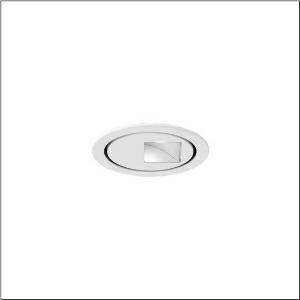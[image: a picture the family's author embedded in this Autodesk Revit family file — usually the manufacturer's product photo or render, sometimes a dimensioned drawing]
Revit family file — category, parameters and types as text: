
# Revit family: lunis_11_micro_round_51dj11cd1wm21
name_source: partatom
category: Lighting Fixtures
units: mm (PartAtom-declared; Revit-internal decimal feet)

## family parameters
Cut with Voids When Loaded = No
Host = Face
Light Source = No
Part Type = Normal
Room Calculation Point = No
Round Connector Dimension = Use Diameter
Shared = No

## types (1)
- Lunis 11 micro round (1 x LED 3000K / CRI = 90 (unbekannt), 1100 lm, 3000K)
    Apparent Load = 20 VA
    CIE Flux Codes = 42 75 96 100 100
    Color Rendering = 90
    Color Temperature = 3000K
    Default Elevation = 1800 mm
    Description = Lunis 11 micro round, downlight, light control with wallwasher, of highly reflective aluminium, highly specular, light emission: direct distribution, LED rated luminous flux: 1.100lm, light colour: 930, with terminal, 5-pole, mains connection: 220..230V, AC, 50/60Hz, LED module, of aluminium, highly specular, white, diameter: 114mm, clamping range: 1..40mm, recessing ring, of plastic, traffic white (RAL 9016), protection rating (complete): IP20, insulation class (complete): insulation class II (safety insulation), certification: CE, permissible ambient temperature for indoor applications: 0..+35°C, packaging unit: 1 piece
    Height = 0 mm  [stored 0 ft]
    Lamp = 1 x LED 3000K / CRI >= 90 (unbekannt)
    Lamp Light Flux = 1100 lm
    Lamp count = 1
    Length = 114 mm
    Luminous efficacy = 56 lm/W
    Manufacturer = Siteco
    ModVariant = No
    Model = 51DJ11CD1WM21
    Mounting Place = Ceiling
    Mounting Type = Recessed
    Number of Poles = 1
    OnlyDefault = Yes
    Power Factor = 1
    Product Name = Lunis 11 micro round
    Product group = downlight
    ProductGroupID = 401
    Protection Class = Protection class II
    Protection Degree = IP 20
    RLX_Detail_Level = 1
    RLX_Emergency_Light_Flux = 0 lm
    RLX_Emergency_Type = 0
    RLX_Emergency_Type_DB = No
    RlxData = <blob elided: 40653 chars, md5=86ec2b00>
    Socket = socket
    Standby Power = 0 W
    System Light Flux = 1100 lm
    System Power = 20 W
    Type Comments = Product without accessories
    Type Image = l_1004773.jpg
    URL = http://relux.com
    VarID = ---
    Voltage = 0 V
    Weight = 0.00 kg
    Width = 114 mm

note: [stored X ft] marks values corroborated as IEEE doubles in the binary element streams (Revit-internal decimal feet)

## geometry (parser evidence)
native form markers: Blend x4, Sweep x8
no freeform markers — native parametric forms only
